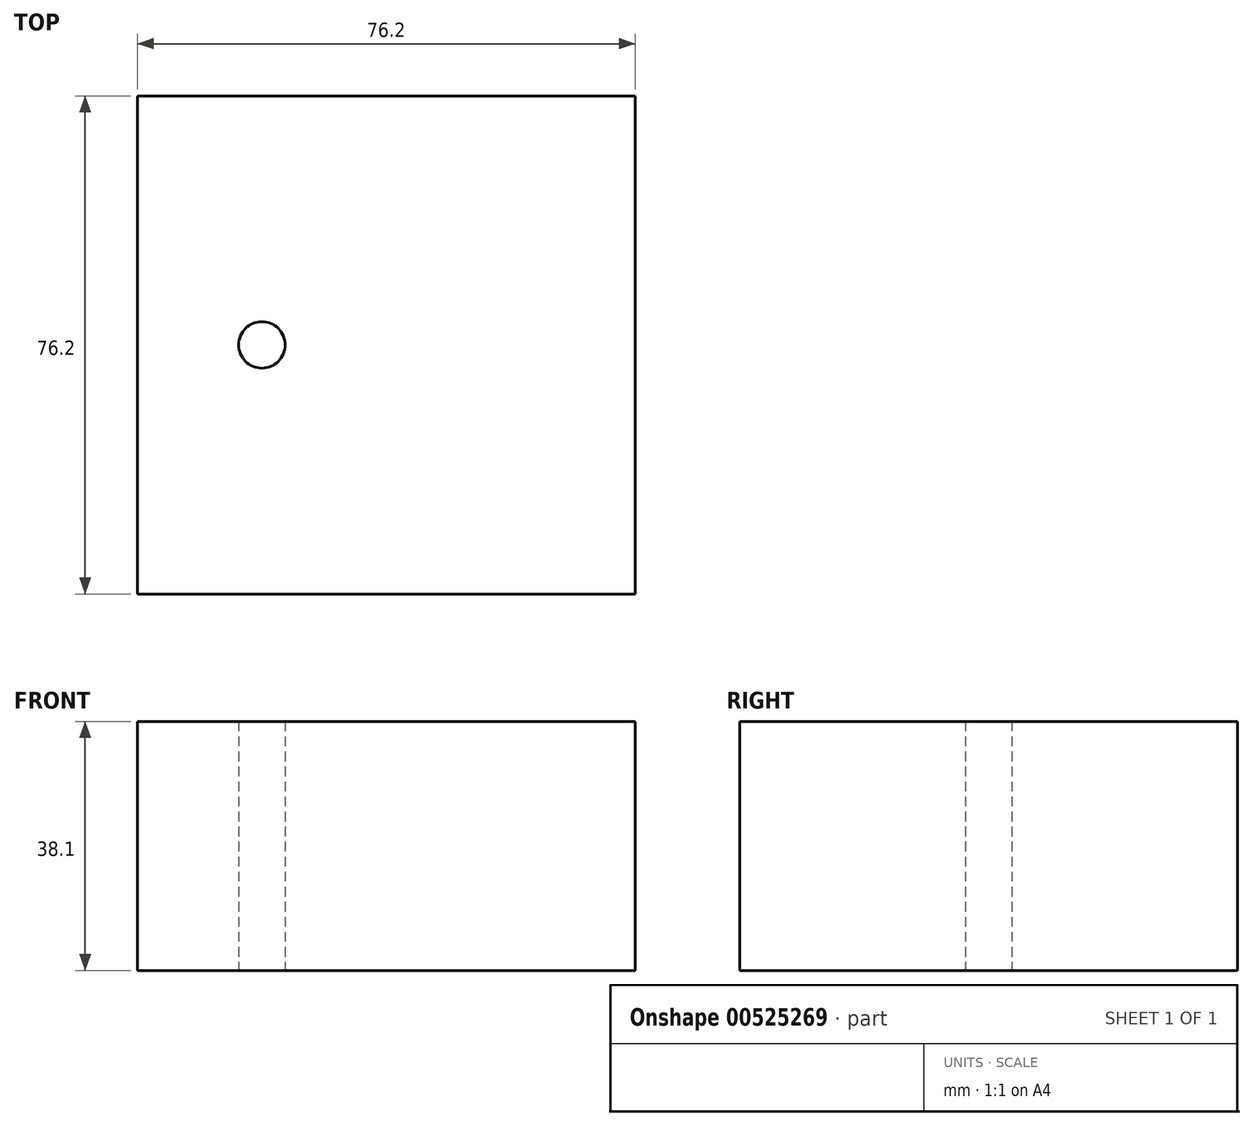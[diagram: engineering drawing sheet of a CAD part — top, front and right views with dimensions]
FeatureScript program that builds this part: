
annotation { "Feature Type Name" : "Feature", "Feature Type Description" : "" }
export const myFeature = defineFeature(function(context is Context, id is Id, definition is map)
    precondition{}
    {
        {
            var Q0;
            Q0=qCreatedBy(makeId("Top.planeOp"),FACE);
            var sketch = newSketch(context, id + "F0", { "sketchPlane" : qUnion([Q0])});
            skLineSegment(sketch, "E0.bottom", {"start": v(38.1, 38.1) * mm, "end": v(-38.1, 38.1) * mm});
            skLineSegment(sketch, "E0.top", {"start": v(38.1, -38.1) * mm, "end": v(-38.1, -38.1) * mm});
            skLineSegment(sketch, "E0.left", {"start": v(38.1, 38.1) * mm, "end": v(38.1, -38.1) * mm});
            skLineSegment(sketch, "E0.right", {"start": v(-38.1, 38.1) * mm, "end": v(-38.1, -38.1) * mm});
            skPoint(sketch, "E0.middle", {"position": v(0, 0) * mm});
            skCircle(sketch, "E1", {"center": v(-19.05, 0) * mm, "radius": 3.56 * mm});
            skSolve(sketch);
        }
        {
            var Q0;
            Q0=makeQuery(id+"F0.imprint","IMPRINT",FACE,{"disambiguationData":[TD([[makeQuery(id+"F0.imprint","IMPRINT",EDGE,{"derivedFrom":sQuery(id+"F0.wireOp",EDGE,"E0.bottom")}),1.0]])]});
            extrude(context, id + "F1", {"entities" : qUnion([Q0]), "depth" : 38.1 * mm, "offsetDistance" : 25.4 * mm});
        }
    });
